# Revit family: novus_montrou_single_lever_bath_and_shower_mixer_71324000
name_source: partatom
category: Plumbing Fixtures
revit_build: Autodesk Revit 2015 (Build: 20140606_1530(x64)
units: mm (PartAtom-declared; Revit-internal decimal feet)

## types (1)
- Chrome 000
    BIMobject category = Taps & Mixers
    BOSUseNativeGeometries = 1
    Brand url = http://www.hansgrohe-int.com
    Default Elevation = 4' - 0"
    Design country = Germany
    EAN code = https://4059625008713
    Edition number = 1
    IFC Classification = Sanitary Terminal
    Installation instructions = https://pro.hansgrohe-int.com
    Manufacturer country = Germany
    Manufacturer name = hansgrohe
    Masterformat 2014 Code = 41 14 33
    Masterformat 2014 Description = Mixers
    Material main = Chrome
    NBS Reference Code = 31-76
    NBS Reference Description = Sanitary Dispensing And Disposal Units
    Nominal height = 0
    Nominal width = 0
    OmniClass Code = 23-11 27 11 39
    OmniClass Description = Watering Equipment
    Product Guid = 96b60429-f647-4abd-81d4-c0e8c554d8c3
    Product SKU = 71324000
    Product data url = https://bimobject.com
    Product family = Novus
    Product group = Bath mixers
    Product name = Novus Montrou single lever bath and shower mixer 71324000
    Product url = https://pro.hansgrohe-int.com
    QR code = http://bimobject.com
    Technical description = https://pro.hansgrohe-int.com
    Uniclass 1.4 Code = L721
    Uniclass 1.4 Description = Sanitary equipment
    Uniclass 2.0 Code = PR-31-76
    Uniclass 2.0 Description = Sanitary Dispensing And Disposal Units
    Uniclass 2015 Code = Pr_40_20_87
    Uniclass 2015 Name = Taps and water supply outlet fittings
    Uniformat II Code = D2010
    Uniformat II Description = Plumbing Fixtures
    Weight Net (Kg) = 0

## geometry (parser evidence)
native form markers: Sweep x2
no freeform markers — native parametric forms only
